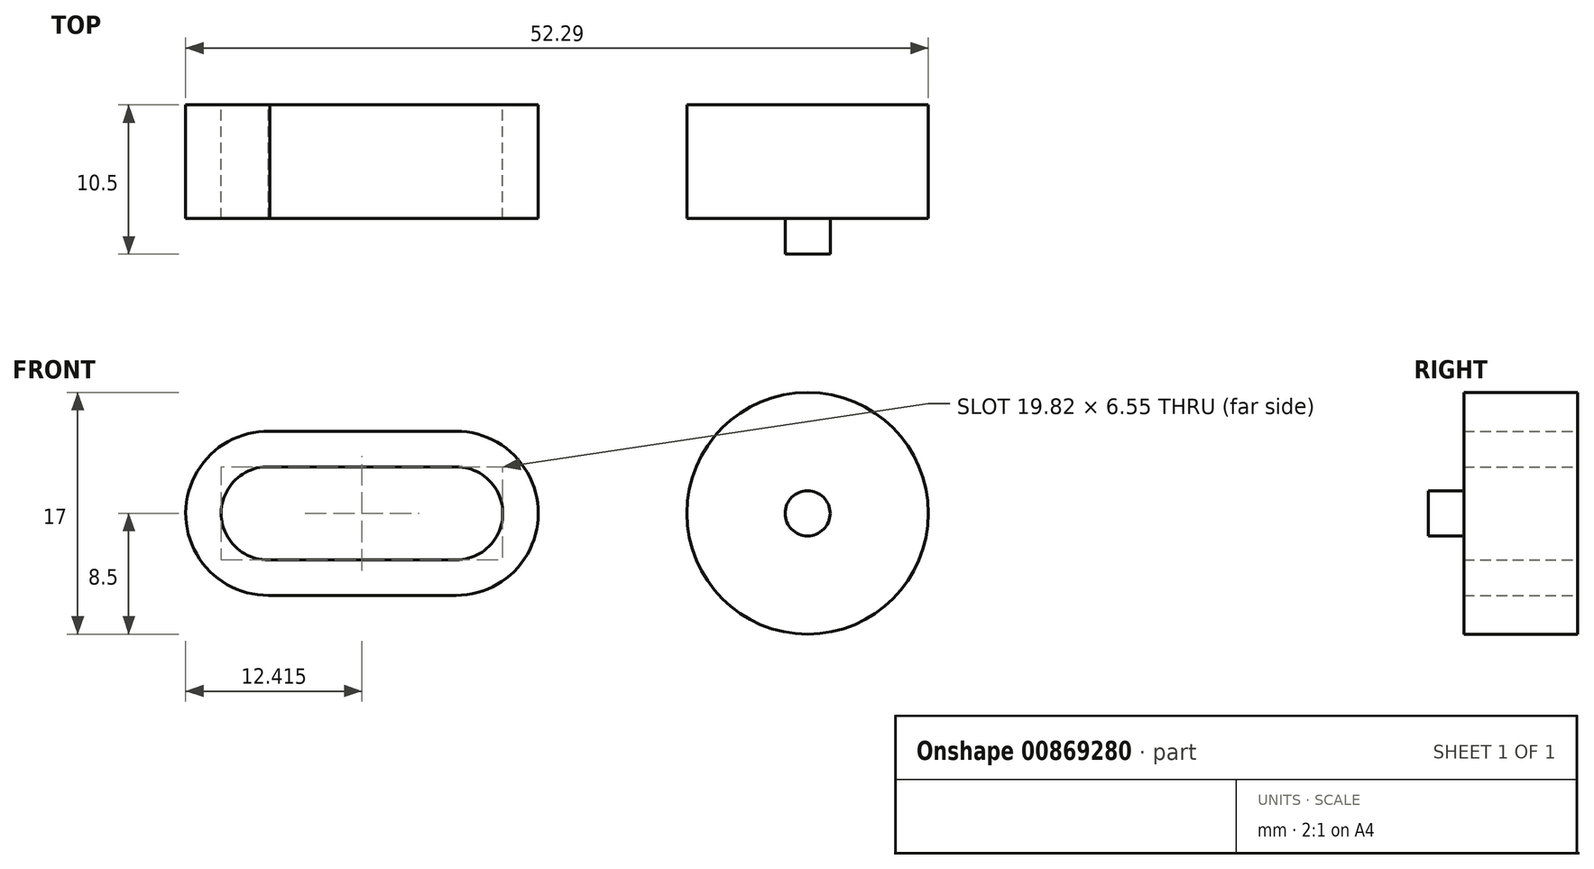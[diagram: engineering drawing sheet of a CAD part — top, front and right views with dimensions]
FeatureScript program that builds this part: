
annotation { "Feature Type Name" : "Feature", "Feature Type Description" : "" }
export const myFeature = defineFeature(function(context is Context, id is Id, definition is map)
    precondition{}
    {
        {
            var Q0;
            Q0=qCreatedBy(makeId("Front.planeOp"),FACE);
            var sketch = newSketch(context, id + "F0", { "sketchPlane" : qUnion([Q0])});
            skCircle(sketch, "E0", {"center": v(0, 0) * mm, "radius": 8.5 * mm});
            skSolve(sketch);
        }
        {
            var Q0;
            Q0 = qSketchRegion(id + "F0", true);
            extrude(context, id + "F1", {"entities" : qUnion([Q0]), "depth" : 8 * mm, "offsetDistance" : 25 * mm});
        }
        {
            var Q0;
            Q0=makeQuery(id+"F1.opExtrude","CAP_FACE",FACE,{"disambiguationData":[OSD([sQuery(id+"F0.wireOp",EDGE,"E0")])],"isStart":false});
            var sketch = newSketch(context, id + "F2", { "sketchPlane" : qUnion([Q0])});
            skCircle(sketch, "E1", {"center": v(0, 0) * mm, "radius": 1.59 * mm});
            skSolve(sketch);
        }
        {
            var Q0;
            Q0=makeQuery(id+"F2.imprint","IMPRINT",FACE,{"disambiguationData":[TD([[makeQuery(id+"F2.imprint","IMPRINT",EDGE,{"derivedFrom":sQuery(id+"F2.wireOp",EDGE,"E1")}),1.0]])]});
            extrude(context, id + "F3", {"entities" : qUnion([Q0]), "operationType" : NewBodyOperationType.ADD, "depth" : 2.5 * mm, "offsetDistance" : 25 * mm});
        }
        {
            var Q0;
            Q0=qCreatedBy(makeId("Front.planeOp"),FACE);
            var sketch = newSketch(context, id + "F4", { "sketchPlane" : qUnion([Q0])});
            skArc(sketch, "E2", {"start": v(-37.9, 3.27) * mm, "mid": v(-41.28, 0.03) * mm, "end": v(-37.97, -3.27) * mm});
            skArc(sketch, "E3", {"start": v(-24.74, -3.27) * mm, "mid": v(-21.47, 0) * mm, "end": v(-24.74, 3.27) * mm});
            skLineSegment(sketch, "E4", {"start": v(-37.9, 3.27) * mm, "end": v(-24.74, 3.27) * mm});
            skLineSegment(sketch, "E5", {"start": v(-37.97, -3.27) * mm, "end": v(-24.74, -3.27) * mm});
            skLineSegment(sketch, "E6.0", {"start": v(-37.96, -5.77) * mm, "end": v(-24.74, -5.77) * mm});
            skArc(sketch, "E6.1", {"start": v(-37.87, 5.77) * mm, "mid": v(-43.78, 0.04) * mm, "end": v(-37.96, -5.77) * mm});
            skLineSegment(sketch, "E6.2", {"start": v(-37.87, 5.77) * mm, "end": v(-24.74, 5.77) * mm});
            skArc(sketch, "E6.3", {"start": v(-24.74, -5.77) * mm, "mid": v(-18.97, 0) * mm, "end": v(-24.74, 5.77) * mm});
            skSolve(sketch);
        }
        {
            var Q0;
            Q0 = qSketchRegion(id + "F4", true);
            extrude(context, id + "F5", {"entities" : qUnion([Q0]), "depth" : 8 * mm, "offsetDistance" : 25 * mm});
        }
    });
